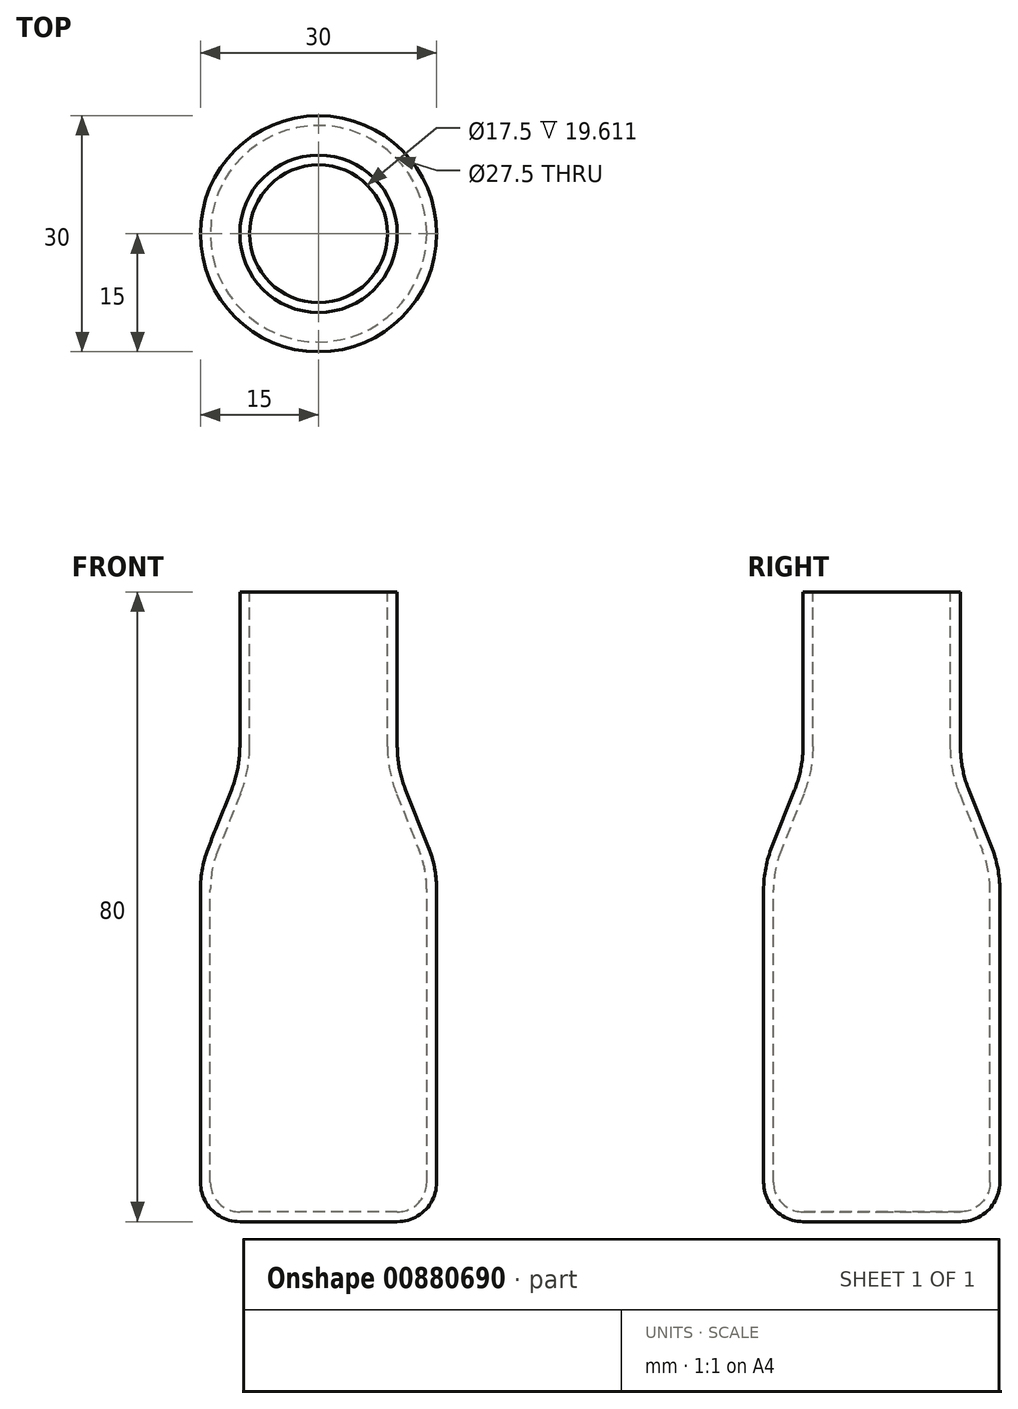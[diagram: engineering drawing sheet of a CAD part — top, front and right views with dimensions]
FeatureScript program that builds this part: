
annotation { "Feature Type Name" : "Feature", "Feature Type Description" : "" }
export const myFeature = defineFeature(function(context is Context, id is Id, definition is map)
    precondition{}
    {
        {
            assignVariable(context, id + "F0", {"name" : "thickness", "anyValue" : 1.25});
        }
        {
            var Q0;
            Q0=qCreatedBy(makeId("Front.planeOp"),FACE);
            var sketch = newSketch(context, id + "F1", { "sketchPlane" : qUnion([Q0])});
            skLineSegment(sketch, "E0.top", {"start": v(0, -20) * mm, "end": v(-15, -20) * mm});
            skLineSegment(sketch, "E0.left", {"start": v(0, 20) * mm, "end": v(0, -20) * mm});
            skLineSegment(sketch, "E0.right", {"start": v(-15, 25) * mm, "end": v(-15, -20) * mm});
            skLineSegment(sketch, "E1", {"start": v(0, 20) * mm, "end": v(0, 60) * mm});
            skLineSegment(sketch, "E2", {"start": v(-10, 37.5) * mm, "end": v(-15, 25) * mm});
            skLineSegment(sketch, "E3.top", {"start": v(0, 60) * mm, "end": v(-10, 60) * mm});
            skLineSegment(sketch, "E3.left", {"start": v(0, 20) * mm, "end": v(0, 60) * mm, "construction": true});
            skLineSegment(sketch, "E3.right", {"start": v(-10, 37.5) * mm, "end": v(-10, 60) * mm});
            skSolve(sketch);
        }
        {
            var Q0;
            Q0 = qSketchRegion(id + "F1", true);
            var Q1;
            Q1=sQuery(id+"F1.wireOp",EDGE,"E0.left");
            revolve(context, id + "F2", {"surfaceOperationType" : NewSurfaceOperationType.NEW, "entities" : qUnion([Q0]), "axis" : qUnion([Q1]), "revolveType" : RevolveType.FULL});
        }
        {
            var Q0;
            Q0=makeQuery(id+"F2.opRevolve","SWEPT_EDGE",EDGE,{"disambiguationData":[OSD([sQuery(id+"F1.wireOp",EDGE,"E0.right"),sQuery(id+"F1.wireOp",EDGE,"E2")])]});
            var Q1;
            Q1=makeQuery(id+"F2.opRevolve","SWEPT_EDGE",EDGE,{"disambiguationData":[OSD([sQuery(id+"F1.wireOp",EDGE,"E2"),sQuery(id+"F1.wireOp",EDGE,"E3.right")])]});
            fillet(context, id + "F3", {"entities" : qUnion([Q0, Q1]), "radius" : 15 * mm, "tangentPropagation" : true, "allowEdgeOverflow" : false});
        }
        {
            var Q0;
            Q0=makeQuery(id+"F2.opRevolve","SWEPT_EDGE",EDGE,{"disambiguationData":[OSD([sQuery(id+"F1.wireOp",EDGE,"E0.top"),sQuery(id+"F1.wireOp",EDGE,"E0.right")])]});
            fillet(context, id + "F4", {"entities" : qUnion([Q0]), "radius" : 5 * mm, "tangentPropagation" : true, "allowEdgeOverflow" : false});
        }
        {
            var Q0;
            Q0=makeQuery(id+"F2.opRevolve","SWEPT_FACE",FACE,{"disambiguationData":[OSD([sQuery(id+"F1.wireOp",EDGE,"E3.top")])]});
            shell(context, id + "F5", {"entities" : qUnion([Q0]), "thickness" : getVariable(context, 'thickness') * mm});
        }
    });
